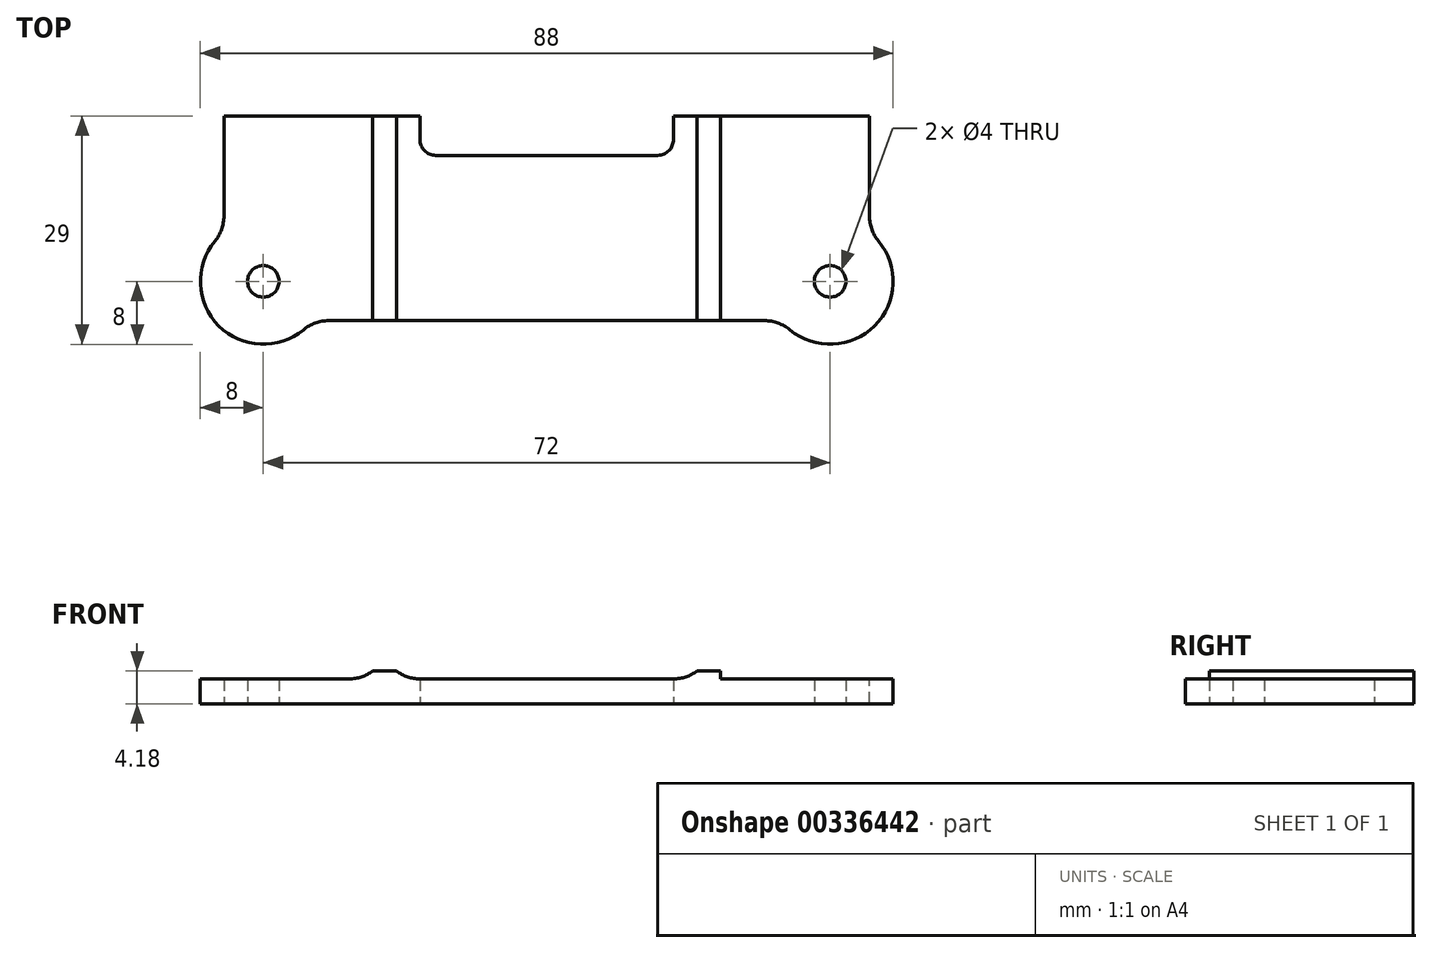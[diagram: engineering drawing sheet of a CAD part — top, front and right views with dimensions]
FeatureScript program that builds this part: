
annotation { "Feature Type Name" : "Feature", "Feature Type Description" : "" }
export const myFeature = defineFeature(function(context is Context, id is Id, definition is map)
    precondition{}
    {
        {
            var Q0;
            Q0=qCreatedBy(makeId("Top.planeOp"),FACE);
            var sketch = newSketch(context, id + "F0", { "sketchPlane" : qUnion([Q0])});
            skLineSegment(sketch, "E0", {"start": v(0, 0) * mm, "end": v(0, 26) * mm});
            skLineSegment(sketch, "E1", {"start": v(0, 26) * mm, "end": v(24.9, 26) * mm});
            skLineSegment(sketch, "E2", {"start": v(24.9, 26) * mm, "end": v(24.9, 21) * mm});
            skLineSegment(sketch, "E3", {"start": v(24.9, 21) * mm, "end": v(41, 21) * mm});
            skLineSegment(sketch, "E4", {"start": v(41, 21) * mm, "end": v(41, 0) * mm, "construction": true});
            skLineSegment(sketch, "E5", {"start": v(41, 0) * mm, "end": v(0, 0) * mm});
            skCircle(sketch, "E6", {"center": v(5, 5) * mm, "radius": 2 * mm});
            skLineSegment(sketch, "E7.MirrorCS", {"start": v(82, 0) * mm, "end": v(82, 26) * mm});
            skLineSegment(sketch, "E8.MirrorCS", {"start": v(82, 26) * mm, "end": v(57.1, 26) * mm});
            skCircle(sketch, "E9.MirrorC", {"center": v(77, 5) * mm, "radius": 2 * mm});
            skLineSegment(sketch, "E10.MirrorCS", {"start": v(57.1, 26) * mm, "end": v(57.1, 21) * mm});
            skLineSegment(sketch, "E11.MirrorCS", {"start": v(57.1, 21) * mm, "end": v(41, 21) * mm});
            skLineSegment(sketch, "E12.MirrorCS", {"start": v(41, 0) * mm, "end": v(82, 0) * mm});
            skArc(sketch, "E13", {"start": v(0, 11.24) * mm, "mid": v(-0.66, -0.66) * mm, "end": v(11.24, 0) * mm});
            skLineSegment(sketch, "E14", {"start": v(0, 11.24) * mm, "end": v(0, 0) * mm, "construction": true});
            skArc(sketch, "E15.MirrorCS", {"start": v(82, 11.24) * mm, "mid": v(82.66, -0.66) * mm, "end": v(70.76, 0) * mm});
            skSolve(sketch);
        }
        {
            var Q0;
            Q0 = qSketchRegion(id + "F0", true);
            extrude(context, id + "F1", {"entities" : qUnion([Q0]), "depth" : 3.17 * mm});
        }
        {
            var Q0;
            Q0=makeQuery(id+"F1.opExtrude","SWEPT_EDGE",EDGE,{"disambiguationData":[OSD([sQuery(id+"F0.wireOp",EDGE,"E5"),sQuery(id+"F0.wireOp",EDGE,"E13")])]});
            var Q1;
            Q1=makeQuery(id+"F1.opExtrude","SWEPT_EDGE",EDGE,{"disambiguationData":[OSD([sQuery(id+"F0.wireOp",EDGE,"E12.MirrorCS"),sQuery(id+"F0.wireOp",EDGE,"E15.MirrorCS")])]});
            var Q2;
            Q2=makeQuery(id+"F1.opExtrude","SWEPT_EDGE",EDGE,{"disambiguationData":[OSD([sQuery(id+"F0.wireOp",EDGE,"E7.MirrorCS"),sQuery(id+"F0.wireOp",EDGE,"E15.MirrorCS")])]});
            var Q3;
            Q3=makeQuery(id+"F1.opExtrude","SWEPT_EDGE",EDGE,{"disambiguationData":[OSD([sQuery(id+"F0.wireOp",EDGE,"E0"),sQuery(id+"F0.wireOp",EDGE,"E13")])]});
            fillet(context, id + "F2", {"entities" : qUnion([Q0, Q1, Q2, Q3]), "radius" : 5 * mm, "tangentPropagation" : true, "allowEdgeOverflow" : false});
        }
        {
            var Q0;
            Q0=makeQuery(id+"F1.opExtrude","SWEPT_EDGE",EDGE,{"disambiguationData":[OSD([sQuery(id+"F0.wireOp",EDGE,"E2"),sQuery(id+"F0.wireOp",EDGE,"E3")])]});
            var Q1;
            Q1=makeQuery(id+"F1.opExtrude","SWEPT_EDGE",EDGE,{"disambiguationData":[OSD([sQuery(id+"F0.wireOp",EDGE,"E10.MirrorCS"),sQuery(id+"F0.wireOp",EDGE,"E11.MirrorCS")])]});
            fillet(context, id + "F3", {"entities" : qUnion([Q0, Q1]), "radius" : 2 * mm, "tangentPropagation" : true, "allowEdgeOverflow" : false});
        }
        {
            var Q0;
            Q0=makeQuery(id+"F1.opExtrude","CAP_FACE",FACE,{"disambiguationData":[OSD([sQuery(id+"F0.wireOp",EDGE,"E0"),sQuery(id+"F0.wireOp",EDGE,"E1"),sQuery(id+"F0.wireOp",EDGE,"E2"),sQuery(id+"F0.wireOp",EDGE,"E3"),sQuery(id+"F0.wireOp",EDGE,"E5"),sQuery(id+"F0.wireOp",EDGE,"E6"),sQuery(id+"F0.wireOp",EDGE,"E7.MirrorCS"),sQuery(id+"F0.wireOp",EDGE,"E8.MirrorCS"),sQuery(id+"F0.wireOp",EDGE,"E9.MirrorC"),sQuery(id+"F0.wireOp",EDGE,"E10.MirrorCS"),sQuery(id+"F0.wireOp",EDGE,"E11.MirrorCS"),sQuery(id+"F0.wireOp",EDGE,"E12.MirrorCS"),sQuery(id+"F0.wireOp",EDGE,"E13"),sQuery(id+"F0.wireOp",EDGE,"E15.MirrorCS")])],"isStart":false});
            var sketch = newSketch(context, id + "F4", { "sketchPlane" : qUnion([Q0])});
            skLineSegment(sketch, "E16", {"start": v(41, 21) * mm, "end": v(41, 0) * mm, "construction": true});
            skLineSegment(sketch, "E17", {"start": v(18.9, 0) * mm, "end": v(18.9, 26) * mm});
            skLineSegment(sketch, "E18", {"start": v(18.9, 26) * mm, "end": v(21.9, 26) * mm});
            skLineSegment(sketch, "E19", {"start": v(21.9, 26) * mm, "end": v(21.9, 0) * mm});
            skLineSegment(sketch, "E20", {"start": v(21.9, 0) * mm, "end": v(18.9, 0) * mm});
            skLineSegment(sketch, "E21.MirrorCS", {"start": v(63.1, 0) * mm, "end": v(63.1, 26) * mm});
            skLineSegment(sketch, "E22.MirrorCS", {"start": v(63.1, 26) * mm, "end": v(60.1, 26) * mm});
            skLineSegment(sketch, "E23.MirrorCS", {"start": v(60.1, 26) * mm, "end": v(60.1, 0) * mm});
            skLineSegment(sketch, "E24.MirrorCS", {"start": v(60.1, 0) * mm, "end": v(63.1, 0) * mm});
            skSolve(sketch);
        }
        {
            var Q0;
            Q0 = qSketchRegion(id + "F4", true);
            extrude(context, id + "F5", {"entities" : qUnion([Q0]), "operationType" : NewBodyOperationType.ADD, "depth" : 1 * mm});
        }
        {
            var Q0;
            Q0=makeQuery(id+"F5.opExtrude","CAP_EDGE",EDGE,{"disambiguationData":[OSD([sQuery(id+"F4.wireOp",EDGE,"E17")])],"isStart":true});
            var Q1;
            Q1=makeQuery(id+"F5.opExtrude","CAP_EDGE",EDGE,{"disambiguationData":[OSD([sQuery(id+"F4.wireOp",EDGE,"E19")])],"isStart":true});
            var Q2;
            Q2=makeQuery(id+"F5.opExtrude","CAP_EDGE",EDGE,{"disambiguationData":[OSD([sQuery(id+"F4.wireOp",EDGE,"E23.MirrorCS")])],"isStart":true});
            var Q3;
            Q3=makeQuery(id+"F5.opExtrude","CAP_EDGE",EDGE,{"disambiguationData":[OSD([sQuery(id+"F4.wireOp",EDGE,"E21.MirrorCS")])],"isStart":true});
            fillet(context, id + "F6", {"entities" : qUnion([Q0, Q1, Q2, Q3]), "radius" : 5 * mm, "tangentPropagation" : true, "allowEdgeOverflow" : false});
        }
    });
